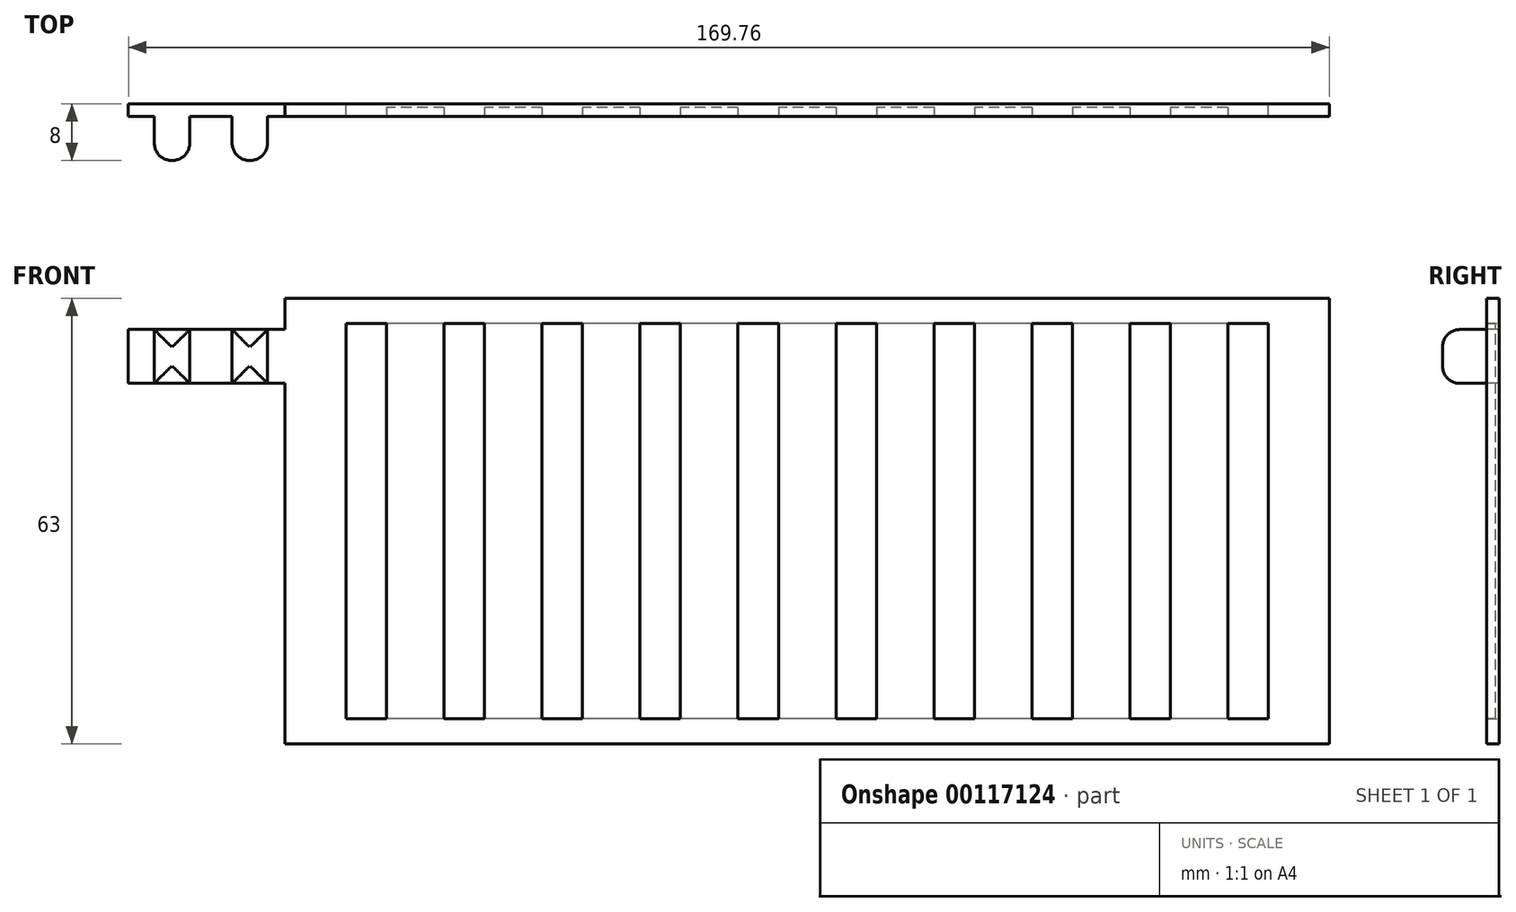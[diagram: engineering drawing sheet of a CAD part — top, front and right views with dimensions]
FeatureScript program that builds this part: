
annotation { "Feature Type Name" : "Feature", "Feature Type Description" : "" }
export const myFeature = defineFeature(function(context is Context, id is Id, definition is map)
    precondition{}
    {
        {
            var Q0;
            Q0=qCreatedBy(makeId("Front.planeOp"),FACE);
            var sketch = newSketch(context, id + "F0", { "sketchPlane" : qUnion([Q0])});
            skLineSegment(sketch, "E0.bottom", {"start": v(73.81, -31.5) * mm, "end": v(-73.81, -31.5) * mm});
            skLineSegment(sketch, "E0.top", {"start": v(73.81, 31.5) * mm, "end": v(-73.81, 31.5) * mm});
            skLineSegment(sketch, "E0.left", {"start": v(73.81, -31.5) * mm, "end": v(73.81, 31.5) * mm});
            skLineSegment(sketch, "E0.right", {"start": v(-73.81, -31.5) * mm, "end": v(-73.81, 31.5) * mm});
            skPoint(sketch, "E0.middle", {"position": v(0, 0) * mm});
            skLineSegment(sketch, "E1.bottom", {"start": v(65.18, -27.94) * mm, "end": v(-65.18, -27.94) * mm});
            skLineSegment(sketch, "E1.top", {"start": v(65.18, 27.94) * mm, "end": v(-65.18, 27.94) * mm});
            skLineSegment(sketch, "E1.left", {"start": v(65.18, -27.94) * mm, "end": v(65.18, 27.94) * mm});
            skLineSegment(sketch, "E1.right", {"start": v(-65.18, -27.94) * mm, "end": v(-65.18, 27.94) * mm});
            skSolve(sketch);
        }
        {
            var Q0;
            Q0=makeQuery(id+"F0.imprint","IMPRINT",FACE,{"disambiguationData":[TD([[makeQuery(id+"F0.imprint","IMPRINT",EDGE,{"derivedFrom":sQuery(id+"F0.wireOp",EDGE,"E0.bottom")}),-1.0]])]});
            extrude(context, id + "F1", {"entities" : qUnion([Q0]), "depth" : 1.78 * mm});
        }
        {
            var Q0;
            Q0=makeQuery(id+"F1.opExtrude","CAP_FACE",FACE,{"disambiguationData":[OSD([sQuery(id+"F0.wireOp",EDGE,"E0.bottom"),sQuery(id+"F0.wireOp",EDGE,"E0.top"),sQuery(id+"F0.wireOp",EDGE,"E0.left"),sQuery(id+"F0.wireOp",EDGE,"E0.right"),sQuery(id+"F0.wireOp",EDGE,"E1.bottom"),sQuery(id+"F0.wireOp",EDGE,"E1.top"),sQuery(id+"F0.wireOp",EDGE,"E1.left"),sQuery(id+"F0.wireOp",EDGE,"E1.right")])],"isStart":false});
            var sketch = newSketch(context, id + "F2", { "sketchPlane" : qUnion([Q0])});
            skLineSegment(sketch, "E2.bottom", {"start": v(-51.33, -27.94) * mm, "end": v(-59.46, -27.94) * mm});
            skLineSegment(sketch, "E2.top", {"start": v(-51.33, 27.94) * mm, "end": v(-59.46, 27.94) * mm});
            skLineSegment(sketch, "E2.left", {"start": v(-51.33, -27.94) * mm, "end": v(-51.33, 27.94) * mm});
            skLineSegment(sketch, "E2.right", {"start": v(-59.46, -27.94) * mm, "end": v(-59.46, 27.94) * mm});
            skPoint(sketch, "E2.middle", {"position": v(-55.4, 0) * mm});
            skLineSegment(sketch, "E3", {"start": v(-65.18, 27.94) * mm, "end": v(-65.18, 47.6) * mm, "construction": true});
            skLineSegment(sketch, "E4", {"start": v(65.18, 27.94) * mm, "end": v(65.18, 47.82) * mm, "construction": true});
            skPoint(sketch, "E5.1.0.0", {"position": v(-41.54, 0) * mm});
            skLineSegment(sketch, "E5.1.0.1", {"start": v(-37.48, -27.94) * mm, "end": v(-45.6, -27.94) * mm});
            skLineSegment(sketch, "E5.1.0.2", {"start": v(-37.48, 27.94) * mm, "end": v(-45.6, 27.94) * mm});
            skLineSegment(sketch, "E5.1.0.3", {"start": v(-37.48, -27.94) * mm, "end": v(-37.48, 27.94) * mm});
            skLineSegment(sketch, "E5.1.0.4", {"start": v(-45.6, -27.94) * mm, "end": v(-45.6, 27.94) * mm});
            skPoint(sketch, "E5.2.0.0", {"position": v(-27.7, 0) * mm});
            skLineSegment(sketch, "E5.2.0.1", {"start": v(-23.63, -27.94) * mm, "end": v(-31.76, -27.94) * mm});
            skLineSegment(sketch, "E5.2.0.2", {"start": v(-23.63, 27.94) * mm, "end": v(-31.76, 27.94) * mm});
            skLineSegment(sketch, "E5.2.0.3", {"start": v(-23.63, -27.94) * mm, "end": v(-23.63, 27.94) * mm});
            skLineSegment(sketch, "E5.2.0.4", {"start": v(-31.76, -27.94) * mm, "end": v(-31.76, 27.94) * mm});
            skPoint(sketch, "E5.3.0.0", {"position": v(-13.85, 0) * mm});
            skLineSegment(sketch, "E5.3.0.1", {"start": v(-9.78, -27.94) * mm, "end": v(-17.91, -27.94) * mm});
            skLineSegment(sketch, "E5.3.0.2", {"start": v(-9.78, 27.94) * mm, "end": v(-17.91, 27.94) * mm});
            skLineSegment(sketch, "E5.3.0.3", {"start": v(-9.78, -27.94) * mm, "end": v(-9.78, 27.94) * mm});
            skLineSegment(sketch, "E5.3.0.4", {"start": v(-17.91, -27.94) * mm, "end": v(-17.91, 27.94) * mm});
            skPoint(sketch, "E5.4.0.0", {"position": v(0, 0) * mm});
            skLineSegment(sketch, "E5.4.0.1", {"start": v(4.06, -27.94) * mm, "end": v(-4.06, -27.94) * mm});
            skLineSegment(sketch, "E5.4.0.2", {"start": v(4.06, 27.94) * mm, "end": v(-4.06, 27.94) * mm});
            skLineSegment(sketch, "E5.4.0.3", {"start": v(4.06, -27.94) * mm, "end": v(4.06, 27.94) * mm});
            skLineSegment(sketch, "E5.4.0.4", {"start": v(-4.06, -27.94) * mm, "end": v(-4.06, 27.94) * mm});
            skPoint(sketch, "E5.5.0.0", {"position": v(13.85, 0) * mm});
            skLineSegment(sketch, "E5.5.0.1", {"start": v(17.91, -27.94) * mm, "end": v(9.78, -27.94) * mm});
            skLineSegment(sketch, "E5.5.0.2", {"start": v(17.91, 27.94) * mm, "end": v(9.78, 27.94) * mm});
            skLineSegment(sketch, "E5.5.0.3", {"start": v(17.91, -27.94) * mm, "end": v(17.91, 27.94) * mm});
            skLineSegment(sketch, "E5.5.0.4", {"start": v(9.78, -27.94) * mm, "end": v(9.78, 27.94) * mm});
            skPoint(sketch, "E5.6.0.0", {"position": v(27.7, 0) * mm});
            skLineSegment(sketch, "E5.6.0.1", {"start": v(31.76, -27.94) * mm, "end": v(23.63, -27.94) * mm});
            skLineSegment(sketch, "E5.6.0.2", {"start": v(31.76, 27.94) * mm, "end": v(23.63, 27.94) * mm});
            skLineSegment(sketch, "E5.6.0.3", {"start": v(31.76, -27.94) * mm, "end": v(31.76, 27.94) * mm});
            skLineSegment(sketch, "E5.6.0.4", {"start": v(23.63, -27.94) * mm, "end": v(23.63, 27.94) * mm});
            skPoint(sketch, "E5.7.0.0", {"position": v(41.54, 0) * mm});
            skLineSegment(sketch, "E5.7.0.1", {"start": v(45.6, -27.94) * mm, "end": v(37.48, -27.94) * mm});
            skLineSegment(sketch, "E5.7.0.2", {"start": v(45.6, 27.94) * mm, "end": v(37.48, 27.94) * mm});
            skLineSegment(sketch, "E5.7.0.3", {"start": v(45.6, -27.94) * mm, "end": v(45.6, 27.94) * mm});
            skLineSegment(sketch, "E5.7.0.4", {"start": v(37.48, -27.94) * mm, "end": v(37.48, 27.94) * mm});
            skPoint(sketch, "E5.8.0.0", {"position": v(55.4, 0) * mm});
            skLineSegment(sketch, "E5.8.0.1", {"start": v(59.46, -27.94) * mm, "end": v(51.33, -27.94) * mm});
            skLineSegment(sketch, "E5.8.0.2", {"start": v(59.46, 27.94) * mm, "end": v(51.33, 27.94) * mm});
            skLineSegment(sketch, "E5.8.0.3", {"start": v(59.46, -27.94) * mm, "end": v(59.46, 27.94) * mm});
            skLineSegment(sketch, "E5.8.0.4", {"start": v(51.33, -27.94) * mm, "end": v(51.33, 27.94) * mm});
            skLineSegment(sketch, "E5.direction1", {"start": v(-59.46, -27.94) * mm, "end": v(-45.6, -27.94) * mm, "construction": true});
            skSolve(sketch);
        }
        {
            var Q0;
            Q0 = qSketchRegion(id + "F2", true);
            extrude(context, id + "F3", {"entities" : qUnion([Q0]), "operationType" : NewBodyOperationType.ADD, "oppositeDirection" : true, "depth" : 1.27 * mm});
        }
        {
            var Q0;
            Q0=makeQuery(id+"F3.boolean.opBoolean","MERGE",FACE,{"derivedFrom":[makeQuery(id+"F1.opExtrude","CAP_FACE",FACE,{"disambiguationData":[OSD([sQuery(id+"F0.wireOp",EDGE,"E0.bottom"),sQuery(id+"F0.wireOp",EDGE,"E0.top"),sQuery(id+"F0.wireOp",EDGE,"E0.left"),sQuery(id+"F0.wireOp",EDGE,"E0.right"),sQuery(id+"F0.wireOp",EDGE,"E1.bottom"),sQuery(id+"F0.wireOp",EDGE,"E1.top"),sQuery(id+"F0.wireOp",EDGE,"E1.left"),sQuery(id+"F0.wireOp",EDGE,"E1.right")])],"isStart":false}),makeQuery(id+"F3.opExtrude","CAP_FACE",FACE,{"disambiguationData":[OSD([sQuery(id+"F2.wireOp",EDGE,"E2.bottom"),sQuery(id+"F2.wireOp",EDGE,"E2.top"),sQuery(id+"F2.wireOp",EDGE,"E2.left"),sQuery(id+"F2.wireOp",EDGE,"E2.right")])],"isStart":true}),makeQuery(id+"F3.opExtrude","CAP_FACE",FACE,{"disambiguationData":[OSD([sQuery(id+"F2.wireOp",EDGE,"E5.1.0.1"),sQuery(id+"F2.wireOp",EDGE,"E5.1.0.2"),sQuery(id+"F2.wireOp",EDGE,"E5.1.0.3"),sQuery(id+"F2.wireOp",EDGE,"E5.1.0.4")])],"isStart":true}),makeQuery(id+"F3.opExtrude","CAP_FACE",FACE,{"disambiguationData":[OSD([sQuery(id+"F2.wireOp",EDGE,"E5.2.0.1"),sQuery(id+"F2.wireOp",EDGE,"E5.2.0.2"),sQuery(id+"F2.wireOp",EDGE,"E5.2.0.3"),sQuery(id+"F2.wireOp",EDGE,"E5.2.0.4")])],"isStart":true}),makeQuery(id+"F3.opExtrude","CAP_FACE",FACE,{"disambiguationData":[OSD([sQuery(id+"F2.wireOp",EDGE,"E5.3.0.1"),sQuery(id+"F2.wireOp",EDGE,"E5.3.0.2"),sQuery(id+"F2.wireOp",EDGE,"E5.3.0.3"),sQuery(id+"F2.wireOp",EDGE,"E5.3.0.4")])],"isStart":true}),makeQuery(id+"F3.opExtrude","CAP_FACE",FACE,{"disambiguationData":[OSD([sQuery(id+"F2.wireOp",EDGE,"E5.4.0.1"),sQuery(id+"F2.wireOp",EDGE,"E5.4.0.2"),sQuery(id+"F2.wireOp",EDGE,"E5.4.0.3"),sQuery(id+"F2.wireOp",EDGE,"E5.4.0.4")])],"isStart":true}),makeQuery(id+"F3.opExtrude","CAP_FACE",FACE,{"disambiguationData":[OSD([sQuery(id+"F2.wireOp",EDGE,"E5.5.0.1"),sQuery(id+"F2.wireOp",EDGE,"E5.5.0.2"),sQuery(id+"F2.wireOp",EDGE,"E5.5.0.3"),sQuery(id+"F2.wireOp",EDGE,"E5.5.0.4")])],"isStart":true}),makeQuery(id+"F3.opExtrude","CAP_FACE",FACE,{"disambiguationData":[OSD([sQuery(id+"F2.wireOp",EDGE,"E5.6.0.1"),sQuery(id+"F2.wireOp",EDGE,"E5.6.0.2"),sQuery(id+"F2.wireOp",EDGE,"E5.6.0.3"),sQuery(id+"F2.wireOp",EDGE,"E5.6.0.4")])],"isStart":true}),makeQuery(id+"F3.opExtrude","CAP_FACE",FACE,{"disambiguationData":[OSD([sQuery(id+"F2.wireOp",EDGE,"E5.7.0.1"),sQuery(id+"F2.wireOp",EDGE,"E5.7.0.2"),sQuery(id+"F2.wireOp",EDGE,"E5.7.0.3"),sQuery(id+"F2.wireOp",EDGE,"E5.7.0.4")])],"isStart":true}),makeQuery(id+"F3.opExtrude","CAP_FACE",FACE,{"disambiguationData":[OSD([sQuery(id+"F2.wireOp",EDGE,"E5.8.0.1"),sQuery(id+"F2.wireOp",EDGE,"E5.8.0.2"),sQuery(id+"F2.wireOp",EDGE,"E5.8.0.3"),sQuery(id+"F2.wireOp",EDGE,"E5.8.0.4")])],"isStart":true})]});
            var sketch = newSketch(context, id + "F4", { "sketchPlane" : qUnion([Q0])});
            skLineSegment(sketch, "E6.left", {"start": v(-65.18, 27.09) * mm, "end": v(-65.18, 19.47) * mm});
            skLineSegment(sketch, "E6.right", {"start": v(-95.95, 27.09) * mm, "end": v(-95.95, 19.47) * mm});
            skLineSegment(sketch, "E7", {"start": v(-95.95, 27.09) * mm, "end": v(-65.18, 27.09) * mm});
            skLineSegment(sketch, "E8", {"start": v(-95.95, 19.47) * mm, "end": v(-65.18, 19.47) * mm});
            skSolve(sketch);
        }
        {
            var Q0;
            Q0 = qSketchRegion(id + "F4", true);
            extrude(context, id + "F5", {"entities" : qUnion([Q0]), "operationType" : NewBodyOperationType.ADD, "oppositeDirection" : true, "depth" : 1.78 * mm});
        }
        {
            var Q0;
            Q0=makeQuery(id+"F5.boolean.opBoolean","MERGE",FACE,{"derivedFrom":[makeQuery(id+"F3.boolean.opBoolean","MERGE",FACE,{"derivedFrom":[makeQuery(id+"F1.opExtrude","CAP_FACE",FACE,{"disambiguationData":[OSD([sQuery(id+"F0.wireOp",EDGE,"E0.bottom"),sQuery(id+"F0.wireOp",EDGE,"E0.top"),sQuery(id+"F0.wireOp",EDGE,"E0.left"),sQuery(id+"F0.wireOp",EDGE,"E0.right"),sQuery(id+"F0.wireOp",EDGE,"E1.bottom"),sQuery(id+"F0.wireOp",EDGE,"E1.top"),sQuery(id+"F0.wireOp",EDGE,"E1.left"),sQuery(id+"F0.wireOp",EDGE,"E1.right")])],"isStart":false}),makeQuery(id+"F3.opExtrude","CAP_FACE",FACE,{"disambiguationData":[OSD([sQuery(id+"F2.wireOp",EDGE,"E2.bottom"),sQuery(id+"F2.wireOp",EDGE,"E2.top"),sQuery(id+"F2.wireOp",EDGE,"E2.left"),sQuery(id+"F2.wireOp",EDGE,"E2.right")])],"isStart":true}),makeQuery(id+"F3.opExtrude","CAP_FACE",FACE,{"disambiguationData":[OSD([sQuery(id+"F2.wireOp",EDGE,"E5.1.0.1"),sQuery(id+"F2.wireOp",EDGE,"E5.1.0.2"),sQuery(id+"F2.wireOp",EDGE,"E5.1.0.3"),sQuery(id+"F2.wireOp",EDGE,"E5.1.0.4")])],"isStart":true}),makeQuery(id+"F3.opExtrude","CAP_FACE",FACE,{"disambiguationData":[OSD([sQuery(id+"F2.wireOp",EDGE,"E5.2.0.1"),sQuery(id+"F2.wireOp",EDGE,"E5.2.0.2"),sQuery(id+"F2.wireOp",EDGE,"E5.2.0.3"),sQuery(id+"F2.wireOp",EDGE,"E5.2.0.4")])],"isStart":true}),makeQuery(id+"F3.opExtrude","CAP_FACE",FACE,{"disambiguationData":[OSD([sQuery(id+"F2.wireOp",EDGE,"E5.3.0.1"),sQuery(id+"F2.wireOp",EDGE,"E5.3.0.2"),sQuery(id+"F2.wireOp",EDGE,"E5.3.0.3"),sQuery(id+"F2.wireOp",EDGE,"E5.3.0.4")])],"isStart":true}),makeQuery(id+"F3.opExtrude","CAP_FACE",FACE,{"disambiguationData":[OSD([sQuery(id+"F2.wireOp",EDGE,"E5.4.0.1"),sQuery(id+"F2.wireOp",EDGE,"E5.4.0.2"),sQuery(id+"F2.wireOp",EDGE,"E5.4.0.3"),sQuery(id+"F2.wireOp",EDGE,"E5.4.0.4")])],"isStart":true}),makeQuery(id+"F3.opExtrude","CAP_FACE",FACE,{"disambiguationData":[OSD([sQuery(id+"F2.wireOp",EDGE,"E5.5.0.1"),sQuery(id+"F2.wireOp",EDGE,"E5.5.0.2"),sQuery(id+"F2.wireOp",EDGE,"E5.5.0.3"),sQuery(id+"F2.wireOp",EDGE,"E5.5.0.4")])],"isStart":true}),makeQuery(id+"F3.opExtrude","CAP_FACE",FACE,{"disambiguationData":[OSD([sQuery(id+"F2.wireOp",EDGE,"E5.6.0.1"),sQuery(id+"F2.wireOp",EDGE,"E5.6.0.2"),sQuery(id+"F2.wireOp",EDGE,"E5.6.0.3"),sQuery(id+"F2.wireOp",EDGE,"E5.6.0.4")])],"isStart":true}),makeQuery(id+"F3.opExtrude","CAP_FACE",FACE,{"disambiguationData":[OSD([sQuery(id+"F2.wireOp",EDGE,"E5.7.0.1"),sQuery(id+"F2.wireOp",EDGE,"E5.7.0.2"),sQuery(id+"F2.wireOp",EDGE,"E5.7.0.3"),sQuery(id+"F2.wireOp",EDGE,"E5.7.0.4")])],"isStart":true}),makeQuery(id+"F3.opExtrude","CAP_FACE",FACE,{"disambiguationData":[OSD([sQuery(id+"F2.wireOp",EDGE,"E5.8.0.1"),sQuery(id+"F2.wireOp",EDGE,"E5.8.0.2"),sQuery(id+"F2.wireOp",EDGE,"E5.8.0.3"),sQuery(id+"F2.wireOp",EDGE,"E5.8.0.4")])],"isStart":true})]}),makeQuery(id+"F5.opExtrude","CAP_FACE",FACE,{"disambiguationData":[OSD([sQuery(id+"F4.wireOp",EDGE,"E6.bottom"),sQuery(id+"F4.wireOp",EDGE,"E6.top"),sQuery(id+"F4.wireOp",EDGE,"E6.left"),sQuery(id+"F4.wireOp",EDGE,"E6.right")])],"isStart":true})]});
            var sketch = newSketch(context, id + "F6", { "sketchPlane" : qUnion([Q0])});
            skSolve(sketch);
        }
        {
            var Q0;
            {var subQ24=sQuery(id+"F0.wireOp",EDGE,"E0.bottom");Q0=makeQuery(id+"F6.imprint","IMPRINT",FACE,{"disambiguationData":[TD([[makeQuery(id+"F6.imprint","IMPRINT",EDGE,{"derivedFrom":makeQuery(id+"F1.opExtrude","CAP_EDGE",EDGE,{"disambiguationData":[OSD([subQ24])],"isStart":false})}),-1.0]])]});}
            var sketch = newSketch(context, id + "F7", { "sketchPlane" : qUnion([Q0])});
            skLineSegment(sketch, "E9.bottom", {"start": v(-87.29, 27.09) * mm, "end": v(-92.29, 27.09) * mm});
            skLineSegment(sketch, "E9.top", {"start": v(-87.29, 19.47) * mm, "end": v(-92.29, 19.47) * mm});
            skLineSegment(sketch, "E9.left", {"start": v(-87.29, 27.09) * mm, "end": v(-87.29, 19.47) * mm});
            skLineSegment(sketch, "E9.right", {"start": v(-92.29, 27.09) * mm, "end": v(-92.29, 19.47) * mm});
            skPoint(sketch, "E9.middle", {"position": v(-89.79, 23.28) * mm});
            skLineSegment(sketch, "E10.bottom", {"start": v(-81.3, 27.09) * mm, "end": v(-76.29, 27.09) * mm});
            skLineSegment(sketch, "E10.top", {"start": v(-81.3, 19.47) * mm, "end": v(-76.29, 19.47) * mm});
            skLineSegment(sketch, "E10.left", {"start": v(-81.3, 27.09) * mm, "end": v(-81.3, 19.47) * mm});
            skLineSegment(sketch, "E10.right", {"start": v(-76.29, 27.09) * mm, "end": v(-76.29, 19.47) * mm});
            skSolve(sketch);
        }
        {
            var Q0;
            Q0 = qSketchRegion(id + "F7", true);
            extrude(context, id + "F8", {"entities" : qUnion([Q0]), "operationType" : NewBodyOperationType.ADD, "depth" : 6.22 * mm});
        }
        {
            var Q0;
            Q0=makeQuery(id+"F8.opExtrude","CAP_FACE",FACE,{"disambiguationData":[OSD([sQuery(id+"F7.wireOp",EDGE,"E9.bottom"),sQuery(id+"F7.wireOp",EDGE,"E9.top"),sQuery(id+"F7.wireOp",EDGE,"E9.left"),sQuery(id+"F7.wireOp",EDGE,"E9.right")])],"isStart":false});
            fillet(context, id + "F9", {"entities" : qUnion([Q0]), "radius" : 2.44 * mm, "tangentPropagation" : true, "allowEdgeOverflow" : false});
        }
        {
            var Q0;
            Q0=makeQuery(id+"F8.opExtrude","CAP_FACE",FACE,{"disambiguationData":[OSD([sQuery(id+"F7.wireOp",EDGE,"E10.bottom"),sQuery(id+"F7.wireOp",EDGE,"E10.top"),sQuery(id+"F7.wireOp",EDGE,"E10.left"),sQuery(id+"F7.wireOp",EDGE,"E10.right")])],"isStart":false});
            fillet(context, id + "F10", {"entities" : qUnion([Q0]), "radius" : 2.44 * mm, "tangentPropagation" : true, "allowEdgeOverflow" : false});
        }
    });
